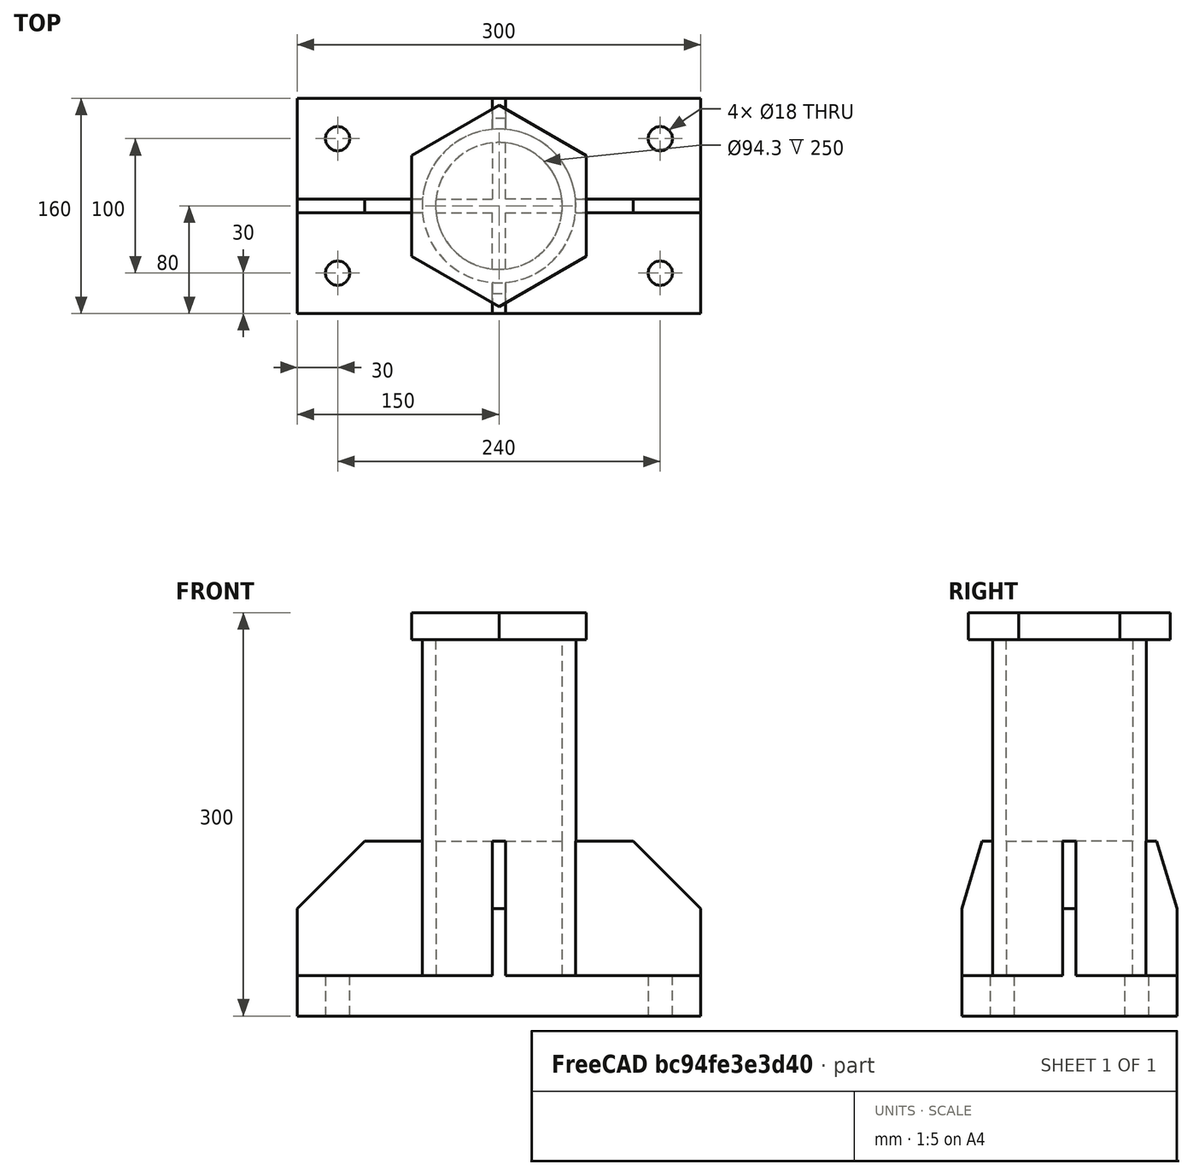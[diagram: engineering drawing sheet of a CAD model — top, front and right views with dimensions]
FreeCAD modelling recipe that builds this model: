
FCSTD DOCUMENT  (FreeCAD 0.21R33694 (Git))
Label: Anschluss_Rahmenfuss_fillet
License: All rights reserved
LicenseURL: http://en.wikipedia.org/wiki/All_rights_reserved
objects: Sketcher::SketchObject×5, Part::Extrusion×5, Fem::ConstraintForce×4, Part::MultiFuse×2, Fem::ConstraintFixed×2, Part::FeaturePython×1, Fem::FemSolverObjectPython×1, App::MaterialObjectPython×1, Part::Fillet×1, Fem::FemMeshObjectPython×1, Fem::FemAnalysis×1
note: 14 computed .brp shape members not serialized (recipe doc carries the construction recipe); baked Part::Feature solids carry a one-line shape summary decoded from their .brp

FEATURE [Sketcher::SketchObject] Sketch
  FullyConstrained = true
  sketch-geometry (12):
    g0: LineSegment StartX=-150 StartY=80 StartZ=0 EndX=150 EndY=80 EndZ=0
    g1: LineSegment StartX=150 StartY=80 StartZ=0 EndX=150 EndY=-80 EndZ=0
    g2: LineSegment StartX=150 StartY=-80 StartZ=0 EndX=-150 EndY=-80 EndZ=0
    g3: LineSegment StartX=-150 StartY=-80 StartZ=0 EndX=-150 EndY=80 EndZ=0
    g4: LineSegment StartX=-120 StartY=50 StartZ=0 EndX=120 EndY=50 EndZ=0
    g5: LineSegment StartX=120 StartY=50 StartZ=0 EndX=120 EndY=-50 EndZ=0
    g6: LineSegment StartX=120 StartY=-50 StartZ=0 EndX=-120 EndY=-50 EndZ=0
    g7: LineSegment StartX=-120 StartY=-50 StartZ=0 EndX=-120 EndY=50 EndZ=0
    g8: Circle CenterX=-120 CenterY=50 CenterZ=0 NormalX=0 NormalY=0 NormalZ=1 AngleXU=0 Radius=9
    g9: Circle CenterX=120 CenterY=50 CenterZ=0 NormalX=0 NormalY=0 NormalZ=1 AngleXU=0 Radius=9
    g10: Circle CenterX=120 CenterY=-50 CenterZ=0 NormalX=0 NormalY=0 NormalZ=1 AngleXU=0 Radius=9
    g11: Circle CenterX=-120 CenterY=-50 CenterZ=0 NormalX=0 NormalY=0 NormalZ=1 AngleXU=0 Radius=9
  constraints (28):
    c: Coincident(g0,g1)
    c: Coincident(g1,g2)
    c: Coincident(g2,g3)
    c: Coincident(g3,g0)
    c: Horizontal(g0)
    c: Vertical(g1)
    c: Symmetric(g2,g1,g-2)
    c: Symmetric(g2,g0,g-1)
    c: DistanceX(g2,g2) = 300
    c: DistanceY(g3,g3) = 160
    c: Coincident(g4,g5)
    c: Coincident(g5,g6)
    c: Coincident(g6,g7)
    c: Coincident(g7,g4)
    c: Horizontal(g4)
    c: Vertical(g5)
    c: Symmetric(g6,g5,g-2)
    c: Symmetric(g6,g4,g-1)
    c: DistanceX(g4,g4) = 240
    c: DistanceY(g5,g5) = 100
    c: Coincident(g8,g4)
    c: Coincident(g9,g4)
    c: Coincident(g10,g5)
    c: Coincident(g11,g6)
    c: Equal(g11,g10)
    c: Equal(g11,g9)
    c: Equal(g11,g8)
    c: Diameter(g11) = 18
FEATURE [Part::Extrusion] Extrude  label="platte"
  Base = -> Sketch
  Dir = (0,0,1)
  DirMode = 0
  FaceMakerClass = Part::FaceMakerBullseye
  LengthFwd = 30
  LengthRev = 0
  Solid = true
  Symmetric = false
FEATURE [Sketcher::SketchObject] Sketch001
  ExternalGeometry = -> [Extrude]
  FullyConstrained = true
  Placement = pos=(0,0,0) rot=(1,0,0;1.5708rad)
  sketch-geometry (6):
    g0: LineSegment StartX=150 StartY=30 StartZ=0 EndX=-150 EndY=30 EndZ=0
    g1: LineSegment StartX=-150 StartY=30 StartZ=0 EndX=-150 EndY=80 EndZ=0
    g2: LineSegment StartX=-150 StartY=80 StartZ=0 EndX=-100 EndY=130 EndZ=0
    g3: LineSegment StartX=-100 StartY=130 StartZ=0 EndX=100 EndY=130 EndZ=0
    g4: LineSegment StartX=100 StartY=130 StartZ=0 EndX=150 EndY=80 EndZ=0
    g5: LineSegment StartX=150 StartY=80 StartZ=0 EndX=150 EndY=30 EndZ=0
  constraints (16):
    c: Coincident(g-3,g0)
    c: Horizontal(g0)
    c: Coincident(g0,g1)
    c: Vertical(g1)
    c: Coincident(g1,g2)
    c: Coincident(g2,g3)
    c: Coincident(g3,g4)
    c: Coincident(g4,g5)
    c: Coincident(g5,g0)
    c: Vertical(g5)
    c: Equal(g1,g5)
    c: DistanceX(g0,g0) = 300
    c: Symmetric(g2,g3,g-2)
    c: DistanceX(g3,g3) = 200
    c: DistanceY(g5,g5) = 50
    c: DistanceY(g0,g3) = 100
FEATURE [Part::Extrusion] Extrude001  label="steife1"
  Base = -> Sketch001
  Dir = (0,-1,-3e-16)
  DirMode = 2
  FaceMakerClass = Part::FaceMakerBullseye
  LengthFwd = 10
  LengthRev = 0
  Solid = true
  Symmetric = true
FEATURE [Sketcher::SketchObject] Sketch002
  FullyConstrained = true
  MapMode = 5
  Placement = pos=(0,0,30) rot=(0,0,1;0rad)
  Support = -> [Extrude]
  sketch-geometry (3):
    g0: Circle CenterX=0 CenterY=0 CenterZ=0 NormalX=0 NormalY=0 NormalZ=1 AngleXU=0 Radius=57.15
    g1: Circle CenterX=0 CenterY=0 CenterZ=0 NormalX=0 NormalY=0 NormalZ=1 AngleXU=0 Radius=47.15
    g2: LineSegment StartX=47.15 StartY=0 StartZ=0 EndX=57.15 EndY=0 EndZ=0
  constraints (8):
    c: Coincident(g0,g-1)
    c: Diameter(g0) = 114.3
    c: Coincident(g1,g0)
    c: PointOnObject(g2,g1)
    c: PointOnObject(g2,g0)
    c: PointOnObject(g2,g-1)
    c: Horizontal(g2)
    c: DistanceX(g2,g2) = 10
FEATURE [Part::Extrusion] Extrude002  label="R114x10"
  Base = -> Sketch002
  Dir = (0,0,1)
  DirMode = 0
  FaceMakerClass = Part::FaceMakerBullseye
  LengthFwd = 270
  LengthRev = 0
  Solid = true
  Symmetric = false
FEATURE [Sketcher::SketchObject] Sketch003
  ExternalGeometry = -> [Extrude,Extrude001]
  FullyConstrained = true
  Placement = pos=(0,0,0) rot=(0.57735,0.57735,0.57735;2.0944rad)
  sketch-geometry (5):
    g0: LineSegment StartX=-80 StartY=30 StartZ=0 EndX=-80 EndY=80 EndZ=0
    g1: LineSegment StartX=-5 StartY=130 StartZ=0 EndX=-5 EndY=30 EndZ=0
    g2: LineSegment StartX=-5 StartY=30 StartZ=0 EndX=-80 EndY=30 EndZ=0
    g3: LineSegment StartX=-80 StartY=80 StartZ=0 EndX=-65 EndY=130 EndZ=0
    g4: LineSegment StartX=-65 StartY=130 StartZ=0 EndX=-5 EndY=130 EndZ=0
  constraints (13):
    c: Vertical(g1)
    c: Coincident(g1,g2)
    c: Coincident(g2,g0)
    c: Vertical(g0)
    c: Horizontal(g2)
    c: Coincident(g0,g3)
    c: Coincident(g3,g4)
    c: Coincident(g4,g1)
    c: Horizontal(g4)
    c: Coincident(g1,g-5)
    c: DistanceY(g0,g0) = 50
    c: DistanceX(g0,g3) = 15
    c: Coincident(g-3,g0)
FEATURE [Part::Extrusion] Extrude003  label="steife2"
  Base = -> Sketch003
  Dir = (1,0,0)
  DirMode = 2
  FaceMakerClass = Part::FaceMakerBullseye
  LengthFwd = 10
  LengthRev = 0
  Solid = true
  Symmetric = true
FEATURE [Part::FeaturePython] Clone  label="steife003"  # Draft clone (typed FeaturePython)
  AttacherType = Attacher::AttachEngine3D
  Fuse = false
  Objects = -> [Extrude003]
  Placement = pos=(0,0,0) rot=(0,0,1;3.14159rad)
  Scale = (1,1,1)
FEATURE [Part::MultiFuse] Fusion  label="bauteil"
  Refine = true
  Shapes = -> [Extrude,Extrude001,Extrude002,Extrude003,Clone]
FEATURE [Sketcher::SketchObject] Sketch004
  FullyConstrained = true
  MapMode = 5
  Placement = pos=(0,0,300) rot=(0,0,1;0rad)
  Support = -> [Fusion]
  sketch-geometry (7):
    g0: LineSegment StartX=65 StartY=37.5278 StartZ=0 EndX=0 EndY=75.0555 EndZ=0
    g1: LineSegment StartX=0 StartY=75.0555 StartZ=0 EndX=-65 EndY=37.5278 EndZ=0
    g2: LineSegment StartX=-65 StartY=37.5278 StartZ=0 EndX=-65 EndY=-37.5278 EndZ=0
    g3: LineSegment StartX=-65 StartY=-37.5278 StartZ=0 EndX=0 EndY=-75.0555 EndZ=0
    g4: LineSegment StartX=0 StartY=-75.0555 StartZ=0 EndX=65 EndY=-37.5278 EndZ=0
    g5: LineSegment StartX=65 StartY=-37.5278 StartZ=0 EndX=65 EndY=37.5278 EndZ=0
    g6: Circle CenterX=0 CenterY=0 CenterZ=0 NormalX=0 NormalY=0 NormalZ=1 AngleXU=0 Radius=75.0555
  constraints (16):
    c: Coincident(g0,g1)
    c: Coincident(g1,g2)
    c: Coincident(g2,g3)
    c: Coincident(g3,g4)
    c: Coincident(g4,g5)
    c: Coincident(g5,g0)
    c: Equal(g0, g1-g5) x5
    c: PointOnObject(g0,g6)
    c: PointOnObject(g1,g6)
    c: PointOnObject(g2,g6)
    c: PointOnObject(g3,g6)
    c: PointOnObject(g4,g6)
    c: PointOnObject(g5,g6)
    c: Coincident(g6,g-1)
    c: Vertical(g5)
    c: DistanceX(g1,g0) = 130
FEATURE [Part::Extrusion] Extrude004  label="lastplatte"
  Base = -> Sketch004
  Dir = (0,0,-1)
  DirMode = 0
  FaceMakerClass = Part::FaceMakerBullseye
  LengthFwd = 20
  LengthRev = 0
  Solid = true
  Symmetric = false
FEATURE [Part::MultiFuse] Fusion001
  Refine = true
  Shapes = -> [Fusion,Extrude004]
FEATURE [Fem::FemSolverObjectPython] SolverCcxTools  # FEM object (typed FeaturePython)
  AnalysisType = 0
  BeamShellResultOutput3D = true
  BucklingFactors = 1
  EigenmodeHighLimit = 1000000
  EigenmodeLowLimit = 0
  EigenmodesCount = 10
  GeometricalNonlinearity = 1
  IterationsControlParameterCutb = 0.25,0.5,0.75,0.85,,,1.5,
  IterationsControlParameterIter = 4,8,9,200,10,400,,200,,
  IterationsControlParameterTimeUse = false
  IterationsThermoMechMaximum = 2000
  IterationsUserDefinedIncrementations = false
  IterationsUserDefinedTimeStepLength = false
  MaterialNonlinearity = 1
  MatrixSolverType = 0
  SplitInputWriter = true
  ThermoMechSteadyState = true
  TimeEnd = 1
  TimeInitialStep = 0.01
FEATURE [App::MaterialObjectPython] MaterialSolid  label="S355"  # material (typed FeaturePython)
  Category = 0
  Material = AuthorAndLicense=(c) 2013 Juergen Riegel (CC-BY 3.0),CardName=CalculiX-Steel,Density=7900 kg/m^3,+8 more (map truncated)
FEATURE [Fem::ConstraintFixed] ConstraintFixed
  NormalDirection = (1,-1e-16,0)
  Normals = (32) [(-1,0,0),(0.5,-0.866025,0),(0.5,0.866025,0),(-1,2.44929e-16,0),(-1,0,0),(0.5,-0.866025,0),(0.5,0.866025,0),(-1,2.44929e-16,0),(-1,0,0),+23 more]
  Points = (32) [(-111,-50,30),(-124.5,-42.2058,30),(-124.5,-57.7942,30),(-111,-50,30),(-111,-50,20),(-124.5,-42.2058,20),(-124.5,-57.7942,20),(-111,-50,20),+24 more]
  References = -> [Fusion001]
  Scale = 5
FEATURE [Fem::ConstraintFixed] ConstraintFixed001
  NormalDirection = (1,-1e-16,0)
  Normals = (32) [(-1,0,0),(0.5,-0.866025,0),(0.5,0.866025,0),(-1,2.44929e-16,0),(-1,0,0),(0.5,-0.866025,0),(0.5,0.866025,0),(-1,2.44929e-16,0),(-1,0,0),+23 more]
  Points = (32) [(129,-50,30),(115.5,-42.2058,30),(115.5,-57.7942,30),(129,-50,30),(129,-50,20),(115.5,-42.2058,20),(115.5,-57.7942,20),(129,-50,20),(129,-50,10),+23 more]
  References = -> [Fusion001]
  Scale = 5
FEATURE [Fem::ConstraintForce] ConstraintForce  label="Q"
  Direction = -> Fusion001 [Edge67]
  DirectionVector = (1,0,0)
  Force = 31900
  NormalDirection = (0,0,1)
  Points = (8) [(-65,-25.0185,300),(-21.6667,-25.0185,300),(21.6667,-25.0185,300),(65,-25.0185,300),(-65,25.0185,300),(-21.6667,25.0185,300),(21.6667,25.0185,300),+1 more]
  References = -> [Fusion001]
  Reversed = true
  Scale = 12
FEATURE [Fem::ConstraintForce] ConstraintForce001  label="N"
  DirectionVector = (0,0,1)
  Force = 40500
  NormalDirection = (0,0,1)
  Points = (8) [(-65,-25.0185,300),(-21.6667,-25.0185,300),(21.6667,-25.0185,300),(65,-25.0185,300),(-65,25.0185,300),(-21.6667,25.0185,300),(21.6667,25.0185,300),+1 more]
  References = -> [Fusion001]
  Scale = 12
FEATURE [Fem::ConstraintForce] ConstraintForce002  label="V1"
  Direction = -> Fusion001 [Edge36]
  DirectionVector = (0,0,-1)
  Force = 96000
  NormalDirection = (1,0,0)
  Points = (12) [(65,-37.5278,280),(65,-12.5093,280),(65,12.5093,280),(65,37.5278,280),(65,-37.5278,290),(65,-12.5093,290),(65,12.5093,290),(65,37.5278,290),+4 more]
  References = -> [Fusion001]
  Reversed = true
  Scale = 6
FEATURE [Fem::ConstraintForce] ConstraintForce003  label="V2"
  Direction = -> Fusion001 [Edge70]
  DirectionVector = (0,0,1)
  Force = 96000
  NormalDirection = (-1,-2e-16,0)
  Points = (12) [(-65,37.5278,280),(-65,12.5093,280),(-65,-12.5093,280),(-65,-37.5278,280),(-65,37.5278,290),(-65,12.5093,290),(-65,-12.5093,290),(-65,-37.5278,290),+4 more]
  References = -> [Fusion001]
  Scale = 6
FEATURE [Part::Fillet] Fillet
  Base = -> Fusion001
  Edges = 1 edges r=1: [Edge27]
FEATURE [Fem::FemMeshObjectPython] FEMMeshGmsh  # FEM object (typed FeaturePython)
  Algorithm2D = 0
  Algorithm3D = 0
  CharacteristicLengthMax = 8
  CharacteristicLengthMin = 0
  CoherenceMesh = true
  ElementDimension = 0
  ElementOrder = 1
  GeometryTolerance = 1e-06
  GroupsOfNodes = false
  HighOrderOptimize = 0
  MeshSizeFromCurvature = 12
  OptimizeNetgen = false
  OptimizeStd = true
  Part = -> Fillet
  RecombinationAlgorithm = 0
  Recombine3DAll = false
  RecombineAll = false
  SecondOrderLinear = false
FEATURE [Fem::FemAnalysis] Analysis
  Group = -> [SolverCcxTools,MaterialSolid,ConstraintFixed,ConstraintFixed001,ConstraintForce,ConstraintForce001,ConstraintForce002,ConstraintForce003,FEMMeshGmsh]
